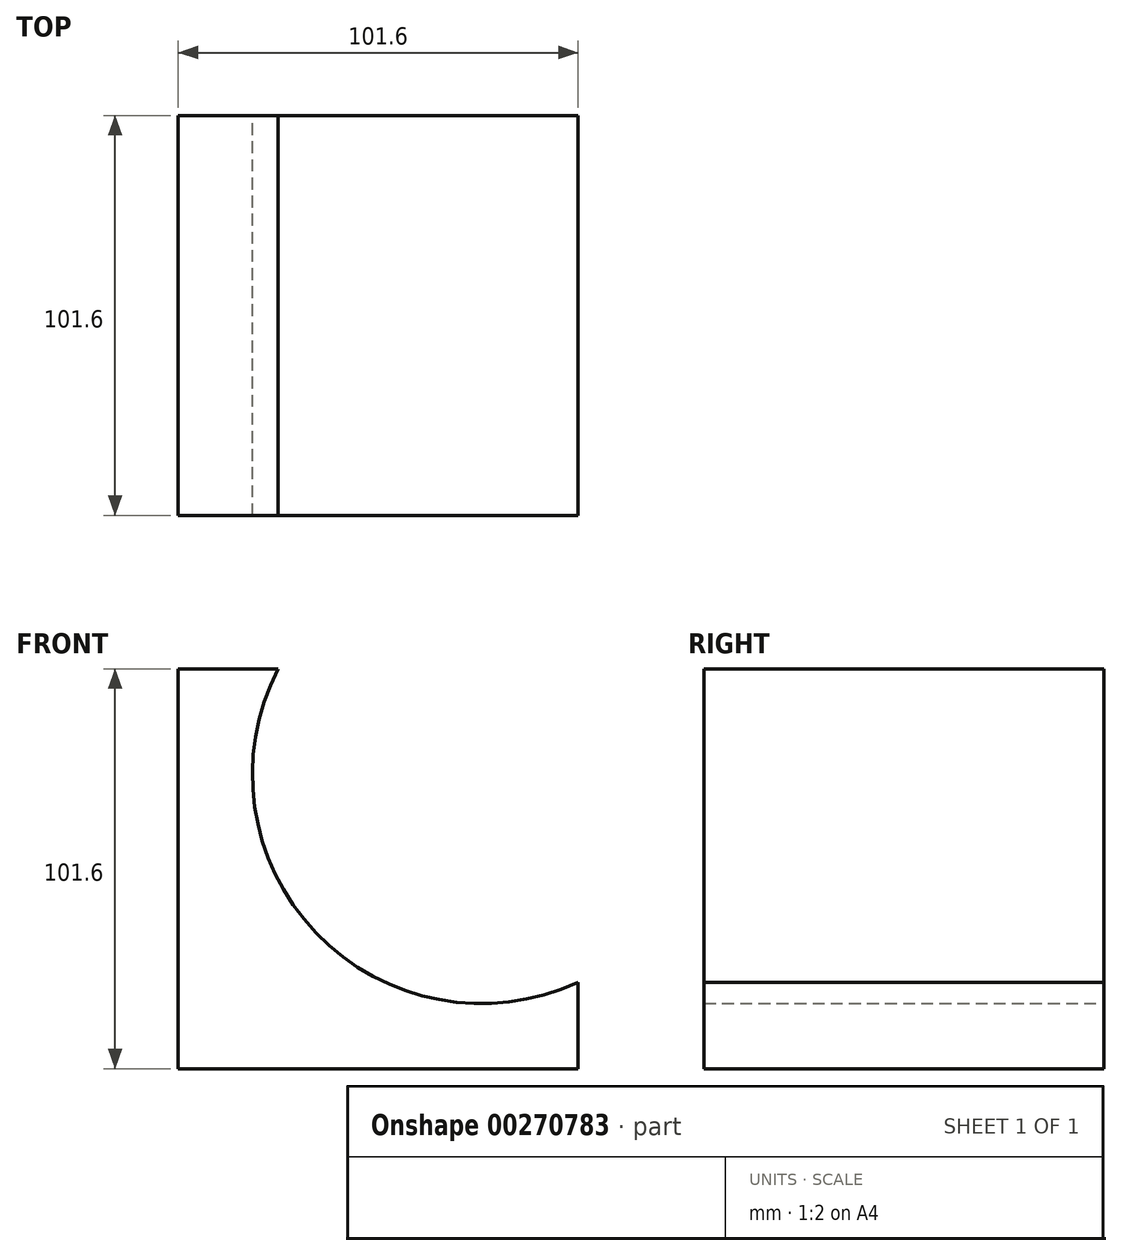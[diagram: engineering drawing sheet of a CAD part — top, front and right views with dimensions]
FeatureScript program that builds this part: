
annotation { "Feature Type Name" : "Feature", "Feature Type Description" : "" }
export const myFeature = defineFeature(function(context is Context, id is Id, definition is map)
    precondition{}
    {
        {
            var Q0;
            Q0=qCreatedBy(makeId("Front.planeOp"),FACE);
            var sketch = newSketch(context, id + "F0", { "sketchPlane" : qUnion([Q0])});
            skLineSegment(sketch, "E0", {"start": v(0, 0) * mm, "end": v(-101.6, 0) * mm});
            skLineSegment(sketch, "E1", {"start": v(-101.6, 0) * mm, "end": v(-101.6, 101.6) * mm});
            skLineSegment(sketch, "E2", {"start": v(-101.6, 101.6) * mm, "end": v(-76.2, 101.6) * mm});
            skLineSegment(sketch, "E3", {"start": v(0, 0) * mm, "end": v(0, 21.96) * mm});
            skArc(sketch, "E4", {"start": v(-76.2, 101.6) * mm, "mid": v(-66.6, 34.51) * mm, "end": v(0, 21.96) * mm});
            skSolve(sketch);
        }
        {
            var Q0;
            Q0 = qSketchRegion(id + "F0", true);
            extrude(context, id + "F1", {"entities" : qUnion([Q0]), "depth" : 101.6 * mm});
        }
    });
